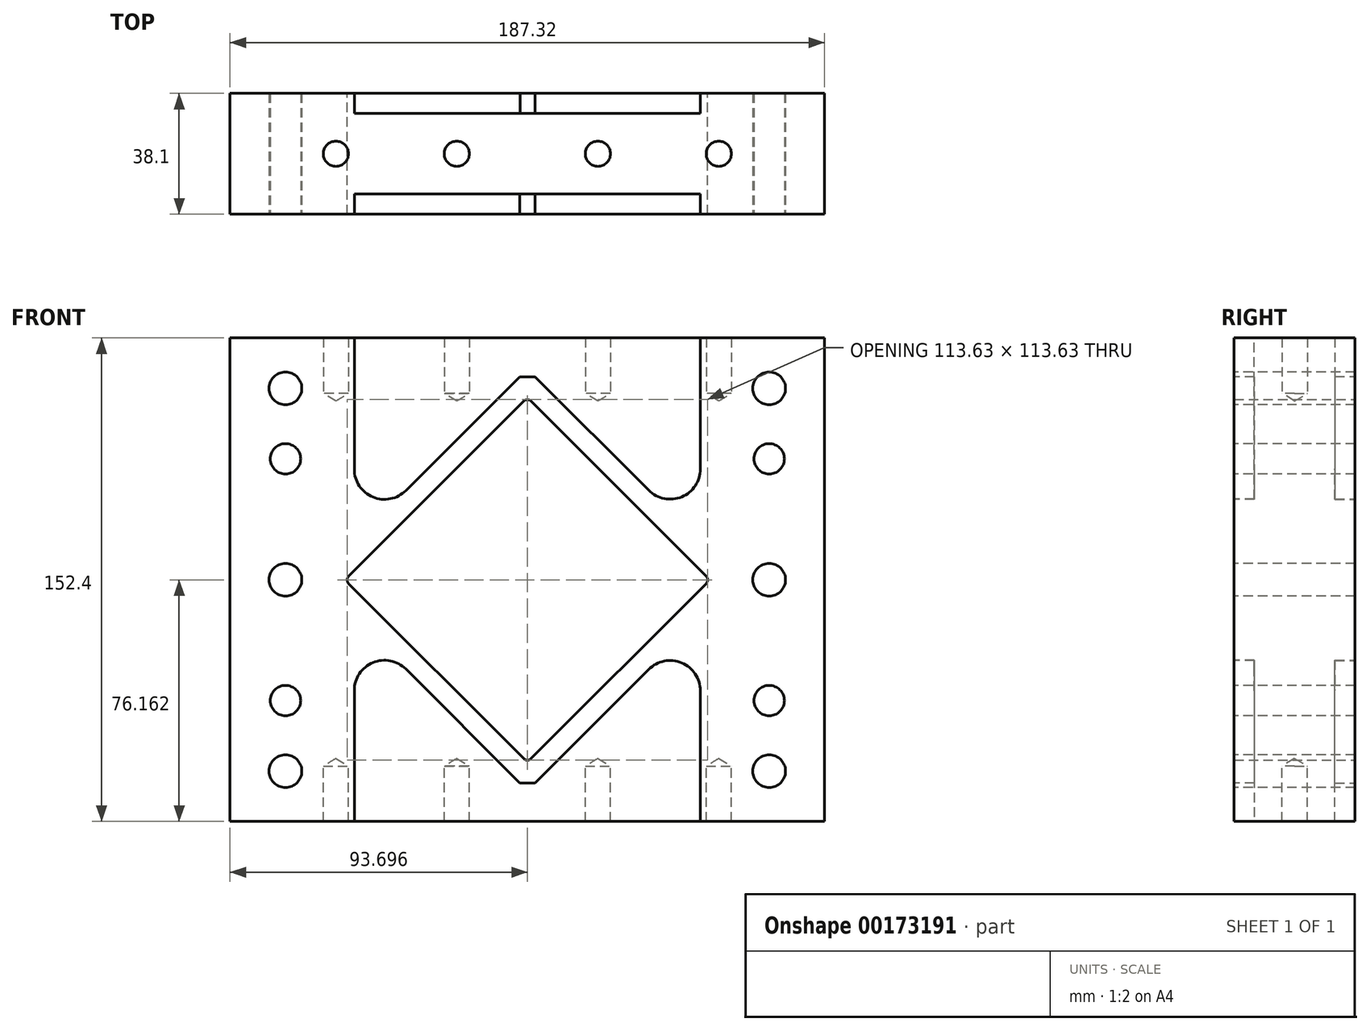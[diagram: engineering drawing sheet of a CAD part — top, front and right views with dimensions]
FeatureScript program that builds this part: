
annotation { "Feature Type Name" : "Feature", "Feature Type Description" : "" }
export const myFeature = defineFeature(function(context is Context, id is Id, definition is map)
    precondition{}
    {
        {
            var Q0;
            Q0=qCreatedBy(makeId("Front.planeOp"),FACE);
            var sketch = newSketch(context, id + "F0", { "sketchPlane" : qUnion([Q0])});
            skLineSegment(sketch, "E0.bottom", {"start": v(-76.3, 64.06) * mm, "end": v(111.02, 64.06) * mm});
            skLineSegment(sketch, "E0.top", {"start": v(-76.3, -88.34) * mm, "end": v(111.02, -88.34) * mm});
            skLineSegment(sketch, "E0.left", {"start": v(-76.3, 64.06) * mm, "end": v(-76.3, -88.34) * mm});
            skLineSegment(sketch, "E0.right", {"start": v(111.02, 64.06) * mm, "end": v(111.02, -88.34) * mm});
            skPoint(sketch, "E1", {"position": v(-58.84, -12.14) * mm});
            skPoint(sketch, "E2", {"position": v(-58.84, -50.24) * mm});
            skPoint(sketch, "E3", {"position": v(-58.84, -72.47) * mm});
            skPoint(sketch, "E4", {"position": v(-58.84, 25.96) * mm});
            skPoint(sketch, "E5", {"position": v(-58.84, 48.18) * mm});
            skPoint(sketch, "E6", {"position": v(93.56, 48.18) * mm});
            skPoint(sketch, "E7", {"position": v(93.56, 25.96) * mm});
            skPoint(sketch, "E8", {"position": v(93.56, -12.14) * mm});
            skPoint(sketch, "E9", {"position": v(93.56, -50.24) * mm});
            skPoint(sketch, "E10", {"position": v(93.56, -72.47) * mm});
            skPoint(sketch, "E11", {"position": v(17.4, -12.18) * mm});
            skLineSegment(sketch, "E12.0", {"start": v(73.75, -13.3) * mm, "end": v(18.52, -68.53) * mm});
            skLineSegment(sketch, "E13.0", {"start": v(-38.96, -13.3) * mm, "end": v(16.27, -68.53) * mm});
            skLineSegment(sketch, "E14.0", {"start": v(18.52, 44.17) * mm, "end": v(73.75, -11.06) * mm});
            skLineSegment(sketch, "E15.trimOffspring", {"start": v(16.27, 44.17) * mm, "end": v(-38.96, -11.06) * mm});
            skPoint(sketch, "E16.visualSharp", {"position": v(17.4, 45.3) * mm});
            skArc(sketch, "E16.filletArc", {"start": v(18.52, 44.17) * mm, "mid": v(17.4, 44.64) * mm, "end": v(16.27, 44.17) * mm});
            skPoint(sketch, "E17.visualSharp", {"position": v(74.87, -12.18) * mm});
            skArc(sketch, "E17.filletArc", {"start": v(73.75, -13.3) * mm, "mid": v(74.21, -12.18) * mm, "end": v(73.75, -11.06) * mm});
            skPoint(sketch, "E18.visualSharp", {"position": v(17.4, -69.65) * mm});
            skArc(sketch, "E18.filletArc", {"start": v(16.27, -68.53) * mm, "mid": v(17.4, -69) * mm, "end": v(18.52, -68.53) * mm});
            skPoint(sketch, "E19.visualSharp", {"position": v(-40.08, -12.18) * mm});
            skArc(sketch, "E19.filletArc", {"start": v(-38.96, -11.06) * mm, "mid": v(-39.42, -12.18) * mm, "end": v(-38.96, -13.3) * mm});
            skLineSegment(sketch, "E20", {"start": v(17.4, -12.18) * mm, "end": v(50.83, -12.18) * mm});
            skLineSegment(sketch, "E21", {"start": v(17.4, -12.18) * mm, "end": v(-12.52, -12.18) * mm});
            skSolve(sketch);
        }
        {
            var Q0;
            Q0=makeQuery(id+"F0.imprint","IMPRINT",FACE,{"disambiguationData":[TD([[makeQuery(id+"F0.imprint","IMPRINT",EDGE,{"derivedFrom":sQuery(id+"F0.wireOp",EDGE,"E0.bottom")}),-1.0]])]});
            extrude(context, id + "F1", {"entities" : qUnion([Q0]), "depth" : 38.1 * mm});
        }
        {
            var Q0;
            Q0=makeQuery(id+"F1.opExtrude","CAP_FACE",FACE,{"disambiguationData":[OSD([sQuery(id+"F0.wireOp",EDGE,"E0.bottom"),sQuery(id+"F0.wireOp",EDGE,"E0.top"),sQuery(id+"F0.wireOp",EDGE,"E0.left"),sQuery(id+"F0.wireOp",EDGE,"E0.right"),sQuery(id+"F0.wireOp",EDGE,"9NI2HCdm-zhV7-IXKU-Ilw0-qgHgseYNw8uk"),sQuery(id+"F0.wireOp",EDGE,"780ab442-0033-43c3-96a2-e75c31360361"),sQuery(id+"F0.wireOp",EDGE,"ca78d6b7-7b32-4318-8b30-639c1e3c6c27"),sQuery(id+"F0.wireOp",EDGE,"23cbe407-0eed-4e64-8f3f-165a4f1e2653"),sQuery(id+"F0.wireOp",EDGE,"2d58fa3e-12f2-48dd-afb8-51d7db77980c"),sQuery(id+"F0.wireOp",EDGE,"b4ce7634-13e8-413b-b57b-a0738a6edea7"),sQuery(id+"F0.wireOp",EDGE,"E12.0"),sQuery(id+"F0.wireOp",EDGE,"E13.0"),sQuery(id+"F0.wireOp",EDGE,"E14.0"),sQuery(id+"F0.wireOp",EDGE,"E15.trimOffspring"),sQuery(id+"F0.wireOp",EDGE,"E16.filletArc"),sQuery(id+"F0.wireOp",EDGE,"E17.filletArc"),sQuery(id+"F0.wireOp",EDGE,"E18.filletArc"),sQuery(id+"F0.wireOp",EDGE,"E19.filletArc")])],"isStart":false});
            var sketch = newSketch(context, id + "F2", { "sketchPlane" : qUnion([Q0])});
            skLineSegment(sketch, "E22.0", {"start": v(14.96, 51.84) * mm, "end": v(-20.9, 15.98) * mm});
            skLineSegment(sketch, "E23.0", {"start": v(19.83, 51.84) * mm, "end": v(55.63, 16.05) * mm});
            skLineSegment(sketch, "E24.0", {"start": v(55.63, -40.4) * mm, "end": v(19.83, -76.2) * mm});
            skLineSegment(sketch, "E25.0", {"start": v(-20.9, -40.33) * mm, "end": v(14.96, -76.2) * mm});
            skLineSegment(sketch, "E26", {"start": v(-76.3, -12.14) * mm, "end": v(111.02, -12.14) * mm});
            skLineSegment(sketch, "E27", {"start": v(17.36, -12.14) * mm, "end": v(17.35, -88.34) * mm});
            skLineSegment(sketch, "E28", {"start": v(17.36, -12.14) * mm, "end": v(17.36, 64.06) * mm});
            skPoint(sketch, "E29.newPointB", {"position": v(-43.51, -6.56) * mm});
            skPoint(sketch, "E30.newPointB", {"position": v(-43.51, -17.8) * mm});
            skPoint(sketch, "E31.visualSharp", {"position": v(78.24, -17.8) * mm});
            skLineSegment(sketch, "E32.0", {"start": v(14.96, 51.84) * mm, "end": v(19.83, 51.84) * mm});
            skPoint(sketch, "E33.orphan", {"position": v(23, 48.66) * mm});
            skLineSegment(sketch, "E34.0", {"start": v(19.83, -76.2) * mm, "end": v(14.96, -76.2) * mm});
            skPoint(sketch, "E35.visualSharp", {"position": v(78.24, -6.56) * mm});
            skLineSegment(sketch, "E36", {"start": v(19.83, 51.84) * mm, "end": v(14.96, 51.84) * mm});
            skLineSegment(sketch, "E37", {"start": v(14.96, -76.2) * mm, "end": v(19.83, -76.2) * mm});
            skLineSegment(sketch, "E38.0", {"start": v(-37.16, 22.71) * mm, "end": v(-37.16, 64.06) * mm});
            skLineSegment(sketch, "E39.0", {"start": v(71.89, 22.78) * mm, "end": v(71.89, 64.06) * mm});
            skLineSegment(sketch, "E40.0", {"start": v(71.89, -47.14) * mm, "end": v(71.89, -88.34) * mm});
            skLineSegment(sketch, "E41.0", {"start": v(-37.16, -47.07) * mm, "end": v(-37.16, -88.34) * mm});
            skPoint(sketch, "E42.MirrorCS.end.orphan", {"position": v(-43.51, -88.34) * mm});
            skPoint(sketch, "E43.MirrorCS.end.orphan", {"position": v(-43.51, 64.06) * mm});
            skPoint(sketch, "E44.end.orphan", {"position": v(78.24, 64.06) * mm});
            skPoint(sketch, "E45.end.orphan", {"position": v(78.24, -88.34) * mm});
            skPoint(sketch, "E46.visualSharp", {"position": v(-37.16, -0.28) * mm});
            skArc(sketch, "E46.filletArc", {"start": v(-37.16, 22.71) * mm, "mid": v(-31.28, 13.91) * mm, "end": v(-20.9, 15.98) * mm});
            skPoint(sketch, "E47.visualSharp", {"position": v(71.89, -0.21) * mm});
            skArc(sketch, "E47.filletArc", {"start": v(55.63, 16.05) * mm, "mid": v(66, 13.98) * mm, "end": v(71.89, 22.78) * mm});
            skPoint(sketch, "E48.visualSharp", {"position": v(71.89, -24.14) * mm});
            skArc(sketch, "E48.filletArc", {"start": v(71.89, -47.14) * mm, "mid": v(66, -38.34) * mm, "end": v(55.63, -40.4) * mm});
            skPoint(sketch, "E49.visualSharp", {"position": v(-37.16, -24.07) * mm});
            skArc(sketch, "E49.filletArc", {"start": v(-20.9, -40.33) * mm, "mid": v(-31.28, -38.27) * mm, "end": v(-37.16, -47.07) * mm});
            skSolve(sketch);
        }
        {
            var Q0;
            Q0=sQuery(id+"F0.wireOp",VERTEX,"E4");
            var Q1;
            Q1=sQuery(id+"F0.wireOp",VERTEX,"E2");
            var Q2;
            Q2=sQuery(id+"F0.wireOp",VERTEX,"E9");
            var Q3;
            Q3=sQuery(id+"F0.wireOp",VERTEX,"E7");
            var Q4;
            Q4=makeQuery(id+"F1.opExtrude","SWEPT_BODY",BODY,{"disambiguationData":[OSD([sQuery(id+"F0.wireOp",EDGE,"E0.bottom"),sQuery(id+"F0.wireOp",EDGE,"E0.top"),sQuery(id+"F0.wireOp",EDGE,"E0.left"),sQuery(id+"F0.wireOp",EDGE,"E0.right"),sQuery(id+"F0.wireOp",EDGE,"9NI2HCdm-zhV7-IXKU-Ilw0-qgHgseYNw8uk"),sQuery(id+"F0.wireOp",EDGE,"780ab442-0033-43c3-96a2-e75c31360361"),sQuery(id+"F0.wireOp",EDGE,"ca78d6b7-7b32-4318-8b30-639c1e3c6c27"),sQuery(id+"F0.wireOp",EDGE,"23cbe407-0eed-4e64-8f3f-165a4f1e2653"),sQuery(id+"F0.wireOp",EDGE,"2d58fa3e-12f2-48dd-afb8-51d7db77980c"),sQuery(id+"F0.wireOp",EDGE,"b4ce7634-13e8-413b-b57b-a0738a6edea7"),sQuery(id+"F0.wireOp",EDGE,"E12.0"),sQuery(id+"F0.wireOp",EDGE,"E13.0"),sQuery(id+"F0.wireOp",EDGE,"E14.0"),sQuery(id+"F0.wireOp",EDGE,"E15.trimOffspring"),sQuery(id+"F0.wireOp",EDGE,"E16.filletArc"),sQuery(id+"F0.wireOp",EDGE,"E17.filletArc"),sQuery(id+"F0.wireOp",EDGE,"E18.filletArc"),sQuery(id+"F0.wireOp",EDGE,"E19.filletArc")])]});
            hole(context, id + "F3", {"style" : HoleStyle.SIMPLE, "endStyle" : HoleEndStyle.THROUGH, "oppositeDirection" : true, "holeDiameter" : 9.58 * mm, "locations" : qUnion([Q0, Q1, Q2, Q3]), "scope" : qUnion([Q4]), "isTappedThrough" : true});
        }
        {
            var Q0;
            {var subQ6=sQuery(id+"F2.wireOp",EDGE,"E22.0");Q0=makeQuery(id+"F2.imprint","IMPRINT",FACE,{"disambiguationData":[TD([[makeQuery(id+"F2.imprint","IMPRINT",EDGE,{"derivedFrom":subQ6}),-1.0]])]});}
            var Q1;
            {var subQ1=sQuery(id+"F2.wireOp",EDGE,"E23.0");Q1=makeQuery(id+"F2.imprint","IMPRINT",FACE,{"disambiguationData":[TD([[makeQuery(id+"F2.imprint","IMPRINT",EDGE,{"derivedFrom":subQ1}),1.0]])]});}
            var Q2;
            {var subQ6=sQuery(id+"F2.wireOp",EDGE,"E24.0");Q2=makeQuery(id+"F2.imprint","IMPRINT",FACE,{"disambiguationData":[TD([[makeQuery(id+"F2.imprint","IMPRINT",EDGE,{"derivedFrom":subQ6}),1.0]])]});}
            var Q3;
            {var subQ6=sQuery(id+"F2.wireOp",EDGE,"E25.0");Q3=makeQuery(id+"F2.imprint","IMPRINT",FACE,{"disambiguationData":[TD([[makeQuery(id+"F2.imprint","IMPRINT",EDGE,{"derivedFrom":subQ6}),-1.0]])]});}
            extrude(context, id + "F4", {"entities" : qUnion([Q0, Q1, Q2, Q3]), "operationType" : NewBodyOperationType.REMOVE, "oppositeDirection" : true, "depth" : 6.35 * mm});
        }
        {
            var Q0;
            Q0=makeQuery(id+"F0.imprint","IMPRINT",FACE,{"disambiguationData":[TD([[makeQuery(id+"F0.imprint","IMPRINT",EDGE,{"derivedFrom":sQuery(id+"F0.wireOp",EDGE,"E0.bottom")}),-1.0]])]});
            var sketch = newSketch(context, id + "F5", { "sketchPlane" : qUnion([Q0])});
            skLineSegment(sketch, "E50.0", {"start": v(19.76, 51.91) * mm, "end": v(55.62, 16.05) * mm});
            skLineSegment(sketch, "E51.0", {"start": v(15.03, 51.91) * mm, "end": v(-20.9, 15.98) * mm});
            skLineSegment(sketch, "E52.0", {"start": v(-76.3, 51.91) * mm, "end": v(-43.5, 51.91) * mm});
            skLineSegment(sketch, "E53.trimOffspring", {"start": v(15.03, 51.91) * mm, "end": v(19.76, 51.91) * mm});
            skPoint(sketch, "E54.endSnap0", {"position": v(-37.63, 7.57) * mm});
            skPoint(sketch, "E55.newPointB", {"position": v(83.65, 6.52) * mm});
            skLineSegment(sketch, "E56.MirrorCS", {"start": v(19.76, -76.27) * mm, "end": v(55.62, -40.4) * mm});
            skLineSegment(sketch, "E57.MirrorCS", {"start": v(15.03, -76.27) * mm, "end": v(19.76, -76.27) * mm});
            skLineSegment(sketch, "E58.MirrorCS", {"start": v(15.03, -76.27) * mm, "end": v(-20.9, -40.34) * mm});
            skLineSegment(sketch, "E59.0", {"start": v(71.88, 64.06) * mm, "end": v(71.88, 22.78) * mm});
            skLineSegment(sketch, "E60.0", {"start": v(-37.16, 64.06) * mm, "end": v(-37.16, 22.72) * mm});
            skLineSegment(sketch, "E61.0", {"start": v(-37.16, -88.41) * mm, "end": v(-37.16, -47.07) * mm});
            skLineSegment(sketch, "E62.0", {"start": v(71.88, -88.41) * mm, "end": v(71.88, -47.14) * mm});
            skPoint(sketch, "E63.orphan", {"position": v(-27.25, -33.99) * mm});
            skPoint(sketch, "E64.orphan", {"position": v(61.97, -34.05) * mm});
            skPoint(sketch, "E65.visualSharp", {"position": v(71.88, -0.21) * mm});
            skArc(sketch, "E65.filletArc", {"start": v(55.62, 16.05) * mm, "mid": v(66, 13.98) * mm, "end": v(71.88, 22.78) * mm});
            skPoint(sketch, "E66.visualSharp", {"position": v(-37.16, -0.28) * mm});
            skArc(sketch, "E66.filletArc", {"start": v(-37.16, 22.72) * mm, "mid": v(-31.28, 13.92) * mm, "end": v(-20.9, 15.98) * mm});
            skPoint(sketch, "E67.visualSharp", {"position": v(-37.16, -24.08) * mm});
            skArc(sketch, "E67.filletArc", {"start": v(-20.9, -40.34) * mm, "mid": v(-31.28, -38.27) * mm, "end": v(-37.16, -47.07) * mm});
            skPoint(sketch, "E68.visualSharp", {"position": v(71.88, -24.14) * mm});
            skArc(sketch, "E68.filletArc", {"start": v(71.88, -47.14) * mm, "mid": v(66, -38.34) * mm, "end": v(55.62, -40.4) * mm});
            skSolve(sketch);
        }
        {
            var Q0;
            Q0=makeQuery(id+"F5.imprint","IMPRINT",FACE,{"disambiguationData":[TD([[makeQuery(id+"F5.imprint","IMPRINT",EDGE,{"derivedFrom":sQuery(id+"F5.wireOp",EDGE,"E50.0")}),1.0]])]});
            var Q1;
            Q1=makeQuery(id+"F5.imprint","IMPRINT",FACE,{"disambiguationData":[TD([[makeQuery(id+"F5.imprint","IMPRINT",EDGE,{"derivedFrom":sQuery(id+"F5.wireOp",EDGE,"E56.MirrorCS")}),-1.0]])]});
            extrude(context, id + "F6", {"entities" : qUnion([Q0, Q1]), "operationType" : NewBodyOperationType.REMOVE, "depth" : 6.35 * mm});
        }
        {
            var Q0;
            Q0=makeQuery(id+"F1.opExtrude","SWEPT_FACE",FACE,{"disambiguationData":[OSD([sQuery(id+"F0.wireOp",EDGE,"E0.top")])]});
            var sketch = newSketch(context, id + "F7", { "sketchPlane" : qUnion([Q0])});
            skLineSegment(sketch, "E69", {"start": v(-76.3, 19.05) * mm, "end": v(111.02, 19.05) * mm});
            skPoint(sketch, "E70.endSnap0", {"position": v(17.36, 31.75) * mm});
            skLineSegment(sketch, "E71", {"start": v(17.36, 6.35) * mm, "end": v(17.36, 31.75) * mm});
            skLineSegment(sketch, "E72.0", {"start": v(39.59, 6.35) * mm, "end": v(39.59, 31.75) * mm});
            skLineSegment(sketch, "E73.0", {"start": v(-4.86, 6.35) * mm, "end": v(-4.86, 31.75) * mm});
            skLineSegment(sketch, "E74.0", {"start": v(77.69, 6.35) * mm, "end": v(77.69, 31.75) * mm});
            skLineSegment(sketch, "E75.0", {"start": v(65.53, -6.35) * mm, "end": v(65.53, 0) * mm});
            skLineSegment(sketch, "E75.1", {"start": v(-82.65, 44.45) * mm, "end": v(-30.81, 44.45) * mm});
            skLineSegment(sketch, "E75.2", {"start": v(-82.65, -6.35) * mm, "end": v(-82.65, 44.45) * mm});
            skLineSegment(sketch, "E75.3", {"start": v(65.53, -6.35) * mm, "end": v(-82.65, -6.35) * mm});
            skLineSegment(sketch, "E75.4", {"start": v(65.53, -6.35) * mm, "end": v(65.53, 0) * mm});
            skLineSegment(sketch, "E75.5", {"start": v(-30.81, 44.45) * mm, "end": v(-30.81, 38.1) * mm});
            skLineSegment(sketch, "E75.6", {"start": v(65.53, 0) * mm, "end": v(65.53, 0) * mm});
            skLineSegment(sketch, "E75.7", {"start": v(-30.81, 38.1) * mm, "end": v(-30.81, 38.1) * mm});
            skLineSegment(sketch, "E75.8", {"start": v(-30.81, 44.45) * mm, "end": v(-30.81, 38.1) * mm});
            skLineSegment(sketch, "E75.9", {"start": v(-30.81, 44.45) * mm, "end": v(117.37, 44.45) * mm});
            skLineSegment(sketch, "E75.10", {"start": v(117.37, 44.45) * mm, "end": v(117.37, -6.35) * mm});
            skLineSegment(sketch, "E75.11", {"start": v(117.37, -6.35) * mm, "end": v(65.53, -6.35) * mm});
            skLineSegment(sketch, "E76.0", {"start": v(-42.96, 6.35) * mm, "end": v(-42.96, 31.75) * mm});
            skPoint(sketch, "E77", {"position": v(-42.96, 19.05) * mm});
            skPoint(sketch, "E78", {"position": v(-4.86, 19.05) * mm});
            skPoint(sketch, "E79", {"position": v(39.59, 19.05) * mm});
            skPoint(sketch, "E80", {"position": v(77.69, 19.05) * mm});
            skSolve(sketch);
        }
        {
            var Q0;
            Q0=sQuery(id+"F7.wireOp",VERTEX,"E77");
            var Q1;
            Q1=sQuery(id+"F7.wireOp",VERTEX,"E78");
            var Q2;
            Q2=sQuery(id+"F7.wireOp",VERTEX,"E80");
            var Q3;
            Q3=sQuery(id+"F7.wireOp",VERTEX,"E79");
            var Q4;
            Q4=makeQuery(id+"F1.opExtrude","SWEPT_BODY",BODY,{"disambiguationData":[OSD([sQuery(id+"F0.wireOp",EDGE,"E0.bottom"),sQuery(id+"F0.wireOp",EDGE,"E0.top"),sQuery(id+"F0.wireOp",EDGE,"E0.left"),sQuery(id+"F0.wireOp",EDGE,"E0.right"),sQuery(id+"F0.wireOp",EDGE,"9NI2HCdm-zhV7-IXKU-Ilw0-qgHgseYNw8uk"),sQuery(id+"F0.wireOp",EDGE,"780ab442-0033-43c3-96a2-e75c31360361"),sQuery(id+"F0.wireOp",EDGE,"ca78d6b7-7b32-4318-8b30-639c1e3c6c27"),sQuery(id+"F0.wireOp",EDGE,"23cbe407-0eed-4e64-8f3f-165a4f1e2653"),sQuery(id+"F0.wireOp",EDGE,"2d58fa3e-12f2-48dd-afb8-51d7db77980c"),sQuery(id+"F0.wireOp",EDGE,"b4ce7634-13e8-413b-b57b-a0738a6edea7"),sQuery(id+"F0.wireOp",EDGE,"E12.0"),sQuery(id+"F0.wireOp",EDGE,"E13.0"),sQuery(id+"F0.wireOp",EDGE,"E14.0"),sQuery(id+"F0.wireOp",EDGE,"E15.trimOffspring"),sQuery(id+"F0.wireOp",EDGE,"E16.filletArc"),sQuery(id+"F0.wireOp",EDGE,"E17.filletArc"),sQuery(id+"F0.wireOp",EDGE,"E18.filletArc"),sQuery(id+"F0.wireOp",EDGE,"E19.filletArc")])]});
            hole(context, id + "F8", {"style" : HoleStyle.SIMPLE, "endStyle" : HoleEndStyle.BLIND, "standardTappedOrClearance" : lookupTablePath({ "standard" : "ANSI", "engagement" : "75%", "pitch" : "16 tpi", "size" : "3/8", "type" : "Tapped" }), "standardBlindInLast" : lookupTablePath({ "standard" : "ANSI", "fit" : "Normal", "engagement" : "75%", "pitch" : "16 tpi", "size" : "3/8", "type" : "Clearance & tapped" }), "holeDiameter" : 7.94 * mm, "majorDiameter" : 9.52 * mm, "showTappedDepth" : true, "holeDepth" : 17.46 * mm, "locations" : qUnion([Q0, Q1, Q2, Q3]), "scope" : qUnion([Q4]), "tappedDepth" : 12.7 * mm, "tapClearance" : 3});
        }
        {
            var Q0;
            Q0=makeQuery(id+"F1.opExtrude","SWEPT_FACE",FACE,{"disambiguationData":[OSD([sQuery(id+"F0.wireOp",EDGE,"E0.bottom")])]});
            var sketch = newSketch(context, id + "F9", { "sketchPlane" : qUnion([Q0])});
            skLineSegment(sketch, "E81", {"start": v(-76.3, -19.05) * mm, "end": v(111.02, -19.05) * mm});
            skLineSegment(sketch, "E82", {"start": v(17.36, -30.06) * mm, "end": v(17.36, -6.35) * mm});
            skPoint(sketch, "E82.startSnap0", {"position": v(17.36, -31.75) * mm});
            skLineSegment(sketch, "E83", {"start": v(39.59, -6.35) * mm, "end": v(39.59, -31.75) * mm});
            skLineSegment(sketch, "E84", {"start": v(-4.86, -6.35) * mm, "end": v(-4.86, -31.75) * mm});
            skLineSegment(sketch, "E85", {"start": v(77.69, -6.35) * mm, "end": v(77.69, -31.75) * mm});
            skLineSegment(sketch, "E86", {"start": v(-42.96, -31.75) * mm, "end": v(-42.96, -6.35) * mm});
            skPoint(sketch, "E87", {"position": v(77.69, -19.05) * mm});
            skPoint(sketch, "E88", {"position": v(39.59, -19.05) * mm});
            skPoint(sketch, "E89", {"position": v(-4.86, -19.05) * mm});
            skPoint(sketch, "E90", {"position": v(-42.96, -19.05) * mm});
            skSolve(sketch);
        }
        {
            var Q0;
            Q0=sQuery(id+"F9.wireOp",VERTEX,"E90");
            var Q1;
            Q1=sQuery(id+"F9.wireOp",VERTEX,"E89");
            var Q2;
            Q2=sQuery(id+"F9.wireOp",VERTEX,"E88");
            var Q3;
            Q3=sQuery(id+"F9.wireOp",VERTEX,"E87");
            var Q4;
            Q4=makeQuery(id+"F1.opExtrude","SWEPT_BODY",BODY,{"disambiguationData":[OSD([sQuery(id+"F0.wireOp",EDGE,"E0.bottom"),sQuery(id+"F0.wireOp",EDGE,"E0.top"),sQuery(id+"F0.wireOp",EDGE,"E0.left"),sQuery(id+"F0.wireOp",EDGE,"E0.right"),sQuery(id+"F0.wireOp",EDGE,"9NI2HCdm-zhV7-IXKU-Ilw0-qgHgseYNw8uk"),sQuery(id+"F0.wireOp",EDGE,"780ab442-0033-43c3-96a2-e75c31360361"),sQuery(id+"F0.wireOp",EDGE,"ca78d6b7-7b32-4318-8b30-639c1e3c6c27"),sQuery(id+"F0.wireOp",EDGE,"23cbe407-0eed-4e64-8f3f-165a4f1e2653"),sQuery(id+"F0.wireOp",EDGE,"2d58fa3e-12f2-48dd-afb8-51d7db77980c"),sQuery(id+"F0.wireOp",EDGE,"b4ce7634-13e8-413b-b57b-a0738a6edea7"),sQuery(id+"F0.wireOp",EDGE,"E12.0"),sQuery(id+"F0.wireOp",EDGE,"E13.0"),sQuery(id+"F0.wireOp",EDGE,"E14.0"),sQuery(id+"F0.wireOp",EDGE,"E15.trimOffspring"),sQuery(id+"F0.wireOp",EDGE,"E16.filletArc"),sQuery(id+"F0.wireOp",EDGE,"E17.filletArc"),sQuery(id+"F0.wireOp",EDGE,"E18.filletArc"),sQuery(id+"F0.wireOp",EDGE,"E19.filletArc")])]});
            hole(context, id + "F10", {"style" : HoleStyle.SIMPLE, "endStyle" : HoleEndStyle.BLIND, "standardTappedOrClearance" : lookupTablePath({ "standard" : "ANSI", "engagement" : "75%", "pitch" : "16 tpi", "size" : "3/8", "type" : "Tapped" }), "standardBlindInLast" : lookupTablePath({ "standard" : "ANSI", "fit" : "Normal", "engagement" : "75%", "pitch" : "16 tpi", "size" : "3/8", "type" : "Clearance & tapped" }), "holeDiameter" : 7.94 * mm, "majorDiameter" : 9.52 * mm, "showTappedDepth" : true, "holeDepth" : 17.46 * mm, "locations" : qUnion([Q0, Q1, Q2, Q3]), "scope" : qUnion([Q4]), "tappedDepth" : 12.7 * mm, "tapClearance" : 3});
        }
        {
            var Q0;
            Q0=sQuery(id+"F0.wireOp",VERTEX,"E3");
            var Q1;
            Q1=sQuery(id+"F0.wireOp",VERTEX,"E1");
            var Q2;
            Q2=sQuery(id+"F0.wireOp",VERTEX,"E5");
            var Q3;
            Q3=sQuery(id+"F0.wireOp",VERTEX,"E6");
            var Q4;
            Q4=sQuery(id+"F0.wireOp",VERTEX,"E8");
            var Q5;
            Q5=sQuery(id+"F0.wireOp",VERTEX,"E10");
            var Q6;
            Q6=makeQuery(id+"F1.opExtrude","SWEPT_BODY",BODY,{"disambiguationData":[OSD([sQuery(id+"F0.wireOp",EDGE,"E0.bottom"),sQuery(id+"F0.wireOp",EDGE,"E0.top"),sQuery(id+"F0.wireOp",EDGE,"E0.left"),sQuery(id+"F0.wireOp",EDGE,"E0.right"),sQuery(id+"F0.wireOp",EDGE,"E12.0"),sQuery(id+"F0.wireOp",EDGE,"E13.0"),sQuery(id+"F0.wireOp",EDGE,"E14.0"),sQuery(id+"F0.wireOp",EDGE,"E15.trimOffspring"),sQuery(id+"F0.wireOp",EDGE,"E16.filletArc"),sQuery(id+"F0.wireOp",EDGE,"E17.filletArc"),sQuery(id+"F0.wireOp",EDGE,"E18.filletArc"),sQuery(id+"F0.wireOp",EDGE,"E19.filletArc")])]});
            hole(context, id + "F11", {"style" : HoleStyle.SIMPLE, "endStyle" : HoleEndStyle.THROUGH, "oppositeDirection" : true, "holeDiameter" : 10.3 * mm, "locations" : qUnion([Q0, Q1, Q2, Q3, Q4, Q5]), "scope" : qUnion([Q6]), "isTappedThrough" : true});
        }
    });
